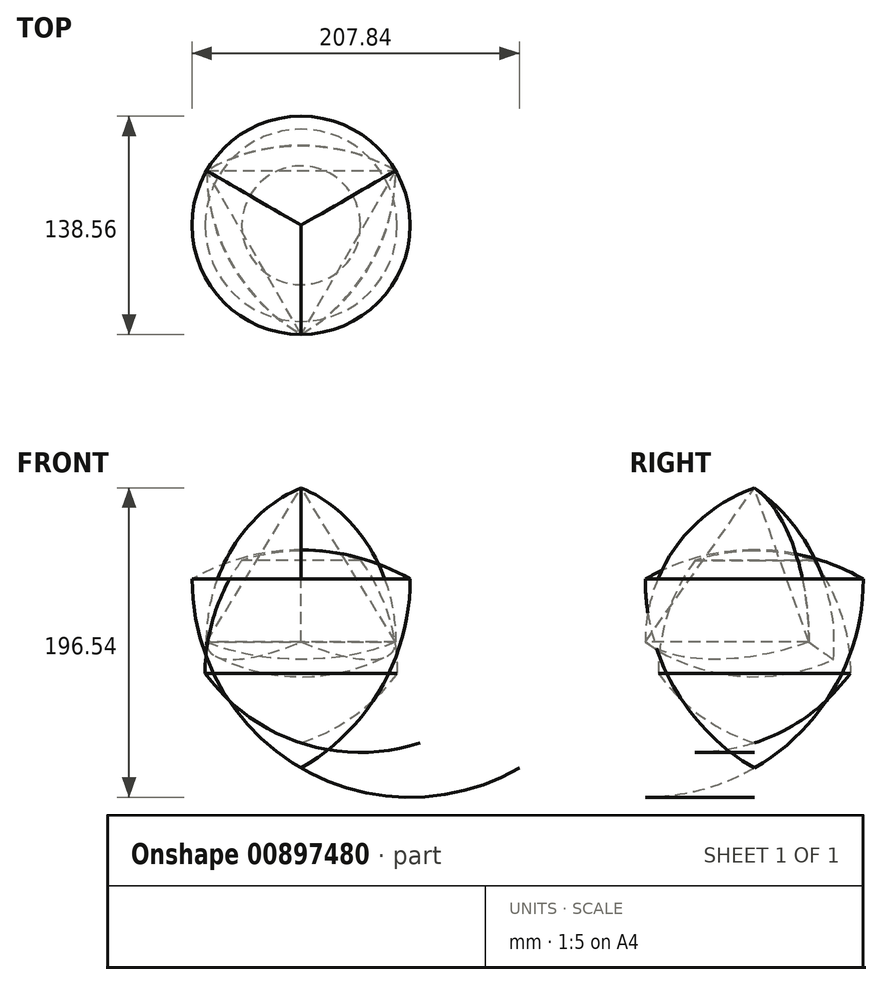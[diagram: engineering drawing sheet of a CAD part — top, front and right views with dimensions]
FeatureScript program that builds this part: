
annotation { "Feature Type Name" : "Feature", "Feature Type Description" : "" }
export const myFeature = defineFeature(function(context is Context, id is Id, definition is map)
    precondition{}
    {
        {
            var Q0;
            Q0=qCreatedBy(makeId("Front.planeOp"),FACE);
            var sketch = newSketch(context, id + "F0", { "sketchPlane" : qUnion([Q0])});
            skPoint(sketch, "E0.0.midPoint", {"position": v(0, 40) * mm});
            skArc(sketch, "E1", {"start": v(0, -80) * mm, "mid": v(50.72, -29.28) * mm, "end": v(69.28, 40) * mm});
            skArc(sketch, "E2", {"start": v(69.28, 40) * mm, "mid": v(0, 58.56) * mm, "end": v(-69.28, 40) * mm});
            skArc(sketch, "E3", {"start": v(-69.28, 40) * mm, "mid": v(-50.72, -29.28) * mm, "end": v(0, -80) * mm});
            skLineSegment(sketch, "E4", {"start": v(0, 58.56) * mm, "end": v(0, -80) * mm});
            skSolve(sketch);
        }
        {
            var Q0;
            Q0=qCreatedBy(makeId("Front.planeOp"),FACE);
            var sketch = newSketch(context, id + "F1", { "sketchPlane" : qUnion([Q0])});
            skLineSegment(sketch, "E5", {"start": v(0, 75.53) * mm, "end": v(0, -80.6) * mm, "construction": true});
            skSolve(sketch);
        }
        {
            var Q0;
            Q0=makeQuery(id+"F0.imprint","IMPRINT",FACE,{"disambiguationData":[TD([[makeQuery(id+"F0.imprint","IMPRINT",EDGE,{"derivedFrom":sQuery(id+"F0.wireOp",EDGE,"E1")}),1.0]])]});
            var Q1;
            Q1=sQuery(id+"F1.wireOp",EDGE,"E5");
            revolve(context, id + "F2", {"surfaceOperationType" : NewSurfaceOperationType.NEW, "entities" : qUnion([Q0]), "axis" : qUnion([Q1]), "revolveType" : RevolveType.FULL});
        }
        {
            var Q0;
            Q0=qCreatedBy(makeId("Front.planeOp"),FACE);
            var sketch = newSketch(context, id + "F3", { "sketchPlane" : qUnion([Q0])});
            skArc(sketch, "E6.cCircle", {"start": v(0, 51.88) * mm, "mid": v(-51.88, 0) * mm, "end": v(0, -51.88) * mm, "construction": true});
            skLineSegment(sketch, "E6.0", {"start": v(-37.7, 51.88) * mm, "end": v(0, 51.88) * mm});
            skLineSegment(sketch, "E6.3", {"start": v(0, -64.12) * mm, "end": v(-60.98, -19.81) * mm});
            skLineSegment(sketch, "E6.4", {"start": v(-60.98, -19.81) * mm, "end": v(-37.7, 51.88) * mm});
            skPoint(sketch, "E6.0.midPoint", {"position": v(0, 51.88) * mm});
            skArc(sketch, "E7", {"start": v(0, -64.12) * mm, "mid": v(34, -46.8) * mm, "end": v(60.98, -19.81) * mm});
            skArc(sketch, "E8.trimOffspring", {"start": v(60.98, -19.81) * mm, "mid": v(55.01, 17.88) * mm, "end": v(37.7, 51.88) * mm});
            skArc(sketch, "E9.trimOffspring", {"start": v(-60.98, -19.81) * mm, "mid": v(-34, -46.8) * mm, "end": v(0, -64.12) * mm});
            skArc(sketch, "E10.trimOffspring", {"start": v(-37.7, 51.88) * mm, "mid": v(-55.01, 17.88) * mm, "end": v(-60.98, -19.81) * mm});
            skArc(sketch, "E11.trimOffspring", {"start": v(37.7, 51.88) * mm, "mid": v(0, 57.85) * mm, "end": v(-37.7, 51.88) * mm});
            skLineSegment(sketch, "E12", {"start": v(0, -64.12) * mm, "end": v(0, 57.85) * mm});
            skSolve(sketch);
        }
        {
            var Q0;
            {var subQ5=sQuery(id+"F3.wireOp",EDGE,"E7");Q0=makeQuery(id+"F3.imprint","IMPRINT",FACE,{"disambiguationData":[TD([[makeQuery(id+"F3.imprint","IMPRINT",EDGE,{"derivedFrom":subQ5}),1.0]])]});}
            var Q1;
            Q1=sQuery(id+"F1.wireOp",EDGE,"E5");
            revolve(context, id + "F4", {"surfaceOperationType" : NewSurfaceOperationType.NEW, "entities" : qUnion([Q0]), "axis" : qUnion([Q1]), "revolveType" : RevolveType.FULL});
        }
        {
            var Q0;
            Q0=qCreatedBy(makeId("Top.planeOp"),FACE);
            var sketch = newSketch(context, id + "F5", { "sketchPlane" : qUnion([Q0])});
            skCircle(sketch, "E13.cCircle", {"center": v(0, 0) * mm, "radius": 34.64 * mm, "construction": true});
            skLineSegment(sketch, "E13.0", {"start": v(-60, 34.64) * mm, "end": v(60, 34.64) * mm});
            skLineSegment(sketch, "E13.1", {"start": v(60, 34.64) * mm, "end": v(0, -69.28) * mm});
            skLineSegment(sketch, "E13.2", {"start": v(0, -69.28) * mm, "end": v(-60, 34.64) * mm});
            skPoint(sketch, "E13.0.midPoint", {"position": v(0, 34.64) * mm});
            skSolve(sketch);
        }
        {
            var Q0;
            Q0=qCreatedBy(makeId("Right.planeOp"),FACE);
            var sketch = newSketch(context, id + "F6", { "sketchPlane" : qUnion([Q0])});
            skPoint(sketch, "E14", {"position": v(0, 97.98) * mm});
            skPoint(sketch, "E15.0", {"position": v(-69.28, 0) * mm});
            skSolve(sketch);
        }
        {
            var Q0;
            Q0=makeQuery(id+"F5.imprint","IMPRINT",FACE,{"disambiguationData":[TD([[makeQuery(id+"F5.imprint","IMPRINT",EDGE,{"derivedFrom":sQuery(id+"F5.wireOp",EDGE,"E13.0")}),-1.0]])]});
            var Q1;
            Q1=sQuery(id+"F6.wireOp",VERTEX,"E14");
            loft(context, id + "F7", {"sheetProfilesArray" : [{ "sheetProfileEntities" : qUnion([Q0]) }, { "sheetProfileEntities" : qUnion([Q1]) }]});
        }
        {
            var Q0;
            {var subQ0=sQuery(id+"F5.wireOp",EDGE,"E13.1");var subQ1=sQuery(id+"F5.wireOp",EDGE,"E13.2");var subQ2=sQuery(id+"F5.wireOp",EDGE,"E13.0");Q0=makeQuery(id+"F7.opLoft","SWEPT_FACE",FACE,{"disambiguationData":[OSD([subQ2,subQ0,subQ1]),TDD([makeQuery(id+"F5.imprint","INTERSECT",VERTEX,{"derivedFrom":[subQ2,subQ0]}),makeQuery(id+"F5.imprint","INTERSECT",VERTEX,{"derivedFrom":[subQ0,subQ1]}),makeQuery(id+"F5.imprint","IMPRINT",EDGE,{"derivedFrom":subQ0})])]});}
            var sketch = newSketch(context, id + "F8", { "sketchPlane" : qUnion([Q0])});
            skArc(sketch, "E16", {"start": v(56.74, -22.68) * mm, "mid": v(52.29, 39.28) * mm, "end": v(17.46, 90.71) * mm});
            skArc(sketch, "E17", {"start": v(17.46, 90.71) * mm, "mid": v(-33.97, 55.88) * mm, "end": v(-61.1, 0) * mm});
            skArc(sketch, "E18.trimOffspring", {"start": v(-61.1, 0) * mm, "mid": v(-5.22, -27.13) * mm, "end": v(56.74, -22.68) * mm});
            skSolve(sketch);
        }
        {
            var Q0;
            Q0=makeQuery(id+"F5.imprint","IMPRINT",FACE,{"disambiguationData":[TD([[makeQuery(id+"F5.imprint","IMPRINT",EDGE,{"derivedFrom":sQuery(id+"F5.wireOp",EDGE,"E13.0")}),-1.0]])]});
            var sketch = newSketch(context, id + "F9", { "sketchPlane" : qUnion([Q0])});
            skLineSegment(sketch, "E19.0.0", {"start": v(-60, 34.64) * mm, "end": v(0, -69.28) * mm});
            skLineSegment(sketch, "E19.0.1", {"start": v(0, -69.28) * mm, "end": v(60, 34.64) * mm});
            skLineSegment(sketch, "E19.0.2", {"start": v(60, 34.64) * mm, "end": v(-60, 34.64) * mm});
            skArc(sketch, "E20", {"start": v(0, -69.28) * mm, "mid": v(43.92, -25.36) * mm, "end": v(60, 34.64) * mm});
            skArc(sketch, "E21.trimOffspring", {"start": v(60, 34.64) * mm, "mid": v(0, 50.72) * mm, "end": v(-60, 34.64) * mm});
            skArc(sketch, "E22.trimOffspring", {"start": v(-60, 34.64) * mm, "mid": v(-43.92, -25.36) * mm, "end": v(0, -69.28) * mm});
            skSolve(sketch);
        }
        {
            var Q0;
            {var subQ0=sQuery(id+"F5.wireOp",EDGE,"E13.0");var subQ1=sQuery(id+"F5.wireOp",EDGE,"E13.1");var subQ2=sQuery(id+"F5.wireOp",EDGE,"E13.2");Q0=makeQuery(id+"F7.opLoft","SWEPT_FACE",FACE,{"disambiguationData":[OSD([subQ0,subQ1,subQ2]),TDD([makeQuery(id+"F5.imprint","INTERSECT",VERTEX,{"derivedFrom":[subQ0,subQ2]}),makeQuery(id+"F5.imprint","INTERSECT",VERTEX,{"derivedFrom":[subQ0,subQ1]}),makeQuery(id+"F5.imprint","IMPRINT",EDGE,{"derivedFrom":subQ0})])]});}
            var sketch = newSketch(context, id + "F10", { "sketchPlane" : qUnion([Q0])});
            skArc(sketch, "E23", {"start": v(0, 92.38) * mm, "mid": v(-43.92, 48.45) * mm, "end": v(-60, -11.55) * mm});
            skArc(sketch, "E24", {"start": v(-60, -11.55) * mm, "mid": v(0, -27.62) * mm, "end": v(60, -11.55) * mm});
            skArc(sketch, "E25.trimOffspring", {"start": v(60, -11.55) * mm, "mid": v(43.92, 48.45) * mm, "end": v(0, 92.38) * mm});
            skSolve(sketch);
        }
        {
            var Q0;
            Q0=makeQuery(id+"F10.imprint","IMPRINT",FACE,{"disambiguationData":[TD([[makeQuery(id+"F10.imprint","IMPRINT",EDGE,{"derivedFrom":sQuery(id+"F10.wireOp",EDGE,"E25.trimOffspring")}),1.0]])]});
            var Q1;
            Q1=sQuery(id+"F10.wireOp",EDGE,"E25.trimOffspring");
            var Q2;
            Q2=sQuery(id+"F8.wireOp",EDGE,"E17");
            var Q3;
            Q3=sQuery(id+"F9.wireOp",EDGE,"E22.trimOffspring");
            sweep(context, id + "F11", {"profiles" : qUnion([Q0]), "surfaceProfiles" : qUnion([Q1, Q2]), "path" : qUnion([Q3])});
        }
        {
            var Q0;
            {var subQ0=sQuery(id+"F5.wireOp",EDGE,"E13.1");var subQ1=sQuery(id+"F5.wireOp",EDGE,"E13.2");var subQ2=sQuery(id+"F5.wireOp",EDGE,"E13.0");Q0=makeQuery(id+"F7.opLoft","SWEPT_FACE",FACE,{"disambiguationData":[OSD([subQ2,subQ0,subQ1]),TDD([makeQuery(id+"F5.imprint","INTERSECT",VERTEX,{"derivedFrom":[subQ2,subQ0]}),makeQuery(id+"F5.imprint","INTERSECT",VERTEX,{"derivedFrom":[subQ0,subQ1]}),makeQuery(id+"F5.imprint","IMPRINT",EDGE,{"derivedFrom":subQ0})])]});}
            var sketch = newSketch(context, id + "F12", { "sketchPlane" : qUnion([Q0])});
            skCircle(sketch, "E26", {"center": v(-61.1, 0) * mm, "radius": 120 * mm});
            skLineSegment(sketch, "E27", {"start": v(-100.38, 113.39) * mm, "end": v(-21.82, -113.39) * mm});
            skSolve(sketch);
        }
        {
            var Q0;
            {var subQ0=sQuery(id+"F5.wireOp",EDGE,"E13.1");var subQ2=sQuery(id+"F5.wireOp",EDGE,"E13.0");var subQ3=sQuery(id+"F6.wireOp",VERTEX,"E14");Q0=makeQuery(id+"F12.imprint","IMPRINT",FACE,{"disambiguationData":[TD([[makeQuery(id+"F12.imprint","IMPRINT",EDGE,{"derivedFrom":makeQuery(id+"F7.opLoft","SWEPT_EDGE",EDGE,{"disambiguationData":[OSD([subQ2,subQ0,subQ3])]})}),1.0]])]});}
            var sketch = newSketch(context, id + "F13", { "sketchPlane" : qUnion([Q0])});
            skPoint(sketch, "E28.0", {"position": v(-61.1, 0) * mm});
            skLineSegment(sketch, "E29.0", {"start": v(56.74, -22.68) * mm, "end": v(17.46, 90.71) * mm});
            skLineSegment(sketch, "E30", {"start": v(-61.1, 0) * mm, "end": v(-74.02, 37.3) * mm});
            skSolve(sketch);
        }
        {
            var Q0;
            {var subQ0=sQuery(id+"F12.wireOp",EDGE,"E27");var subQ1=sQuery(id+"F12.wireOp",EDGE,"E26");var subQ2=makeQuery(id+"F12.imprint","INTERSECT",VERTEX,{"disambiguationData":[OD(0.0)],"derivedFrom":[subQ1,subQ0]});Q0=makeQuery(id+"F12.imprint","IMPRINT",FACE,{"disambiguationData":[TD([[makeQuery(id+"F12.imprint","IMPRINT",EDGE,{"disambiguationData":[TD([[subQ2,-1.0]])],"derivedFrom":subQ1}),1.0]])]});}
            var Q1;
            Q1=sQuery(id+"F13.wireOp",EDGE,"E30");
            revolve(context, id + "F14", {"surfaceOperationType" : NewSurfaceOperationType.NEW, "entities" : qUnion([Q0]), "axis" : qUnion([Q1]), "revolveType" : RevolveType.FULL});
        }
        {
            var Q0;
            {var subQ0=sQuery(id+"F5.wireOp",EDGE,"E13.0");var subQ1=sQuery(id+"F5.wireOp",EDGE,"E13.1");var subQ2=sQuery(id+"F5.wireOp",EDGE,"E13.2");Q0=makeQuery(id+"F7.opLoft","SWEPT_FACE",FACE,{"disambiguationData":[OSD([subQ0,subQ1,subQ2]),TDD([makeQuery(id+"F5.imprint","INTERSECT",VERTEX,{"derivedFrom":[subQ0,subQ2]}),makeQuery(id+"F5.imprint","INTERSECT",VERTEX,{"derivedFrom":[subQ0,subQ1]}),makeQuery(id+"F5.imprint","IMPRINT",EDGE,{"derivedFrom":subQ0})])]});}
            var sketch = newSketch(context, id + "F15", { "sketchPlane" : qUnion([Q0])});
            skCircle(sketch, "E31", {"center": v(-60, -11.55) * mm, "radius": 120 * mm});
            skLineSegment(sketch, "E32", {"start": v(0, 92.38) * mm, "end": v(-120, -115.47) * mm});
            skSolve(sketch);
        }
        {
            var Q0;
            {var subQ0=sQuery(id+"F15.wireOp",EDGE,"E32");var subQ1=sQuery(id+"F15.wireOp",EDGE,"E31");var subQ5=makeQuery(id+"F15.imprint","INTERSECT",VERTEX,{"derivedFrom":[subQ1,subQ0]});Q0=makeQuery(id+"F15.imprint","IMPRINT",FACE,{"disambiguationData":[TD([[makeQuery(id+"F15.imprint","IMPRINT",EDGE,{"disambiguationData":[TD([[subQ5,1.0]])],"derivedFrom":subQ1}),1.0]])]});}
            var Q1;
            Q1=sQuery(id+"F15.wireOp",EDGE,"E32");
            revolve(context, id + "F16", {"surfaceOperationType" : NewSurfaceOperationType.NEW, "entities" : qUnion([Q0]), "axis" : qUnion([Q1]), "revolveType" : RevolveType.FULL});
        }
        {
            var Q0;
            {var subQ0=sQuery(id+"F5.wireOp",EDGE,"E13.2");var subQ1=sQuery(id+"F5.wireOp",EDGE,"E13.1");var subQ2=sQuery(id+"F5.wireOp",EDGE,"E13.0");Q0=makeQuery(id+"F7.opLoft","SWEPT_FACE",FACE,{"disambiguationData":[OSD([subQ2,subQ1,subQ0]),TDD([makeQuery(id+"F5.imprint","INTERSECT",VERTEX,{"derivedFrom":[subQ2,subQ0]}),makeQuery(id+"F5.imprint","INTERSECT",VERTEX,{"derivedFrom":[subQ1,subQ0]}),makeQuery(id+"F5.imprint","IMPRINT",EDGE,{"derivedFrom":subQ0})])]});}
            var sketch = newSketch(context, id + "F17", { "sketchPlane" : qUnion([Q0])});
            skCircle(sketch, "E33", {"center": v(-56.74, -22.68) * mm, "radius": 120 * mm});
            skLineSegment(sketch, "E34", {"start": v(-17.46, 90.71) * mm, "end": v(-96.02, -136.07) * mm});
            skSolve(sketch);
        }
        {
            var Q0;
            {var subQ0=sQuery(id+"F17.wireOp",EDGE,"E34");var subQ1=sQuery(id+"F17.wireOp",EDGE,"E33");var subQ5=makeQuery(id+"F17.imprint","INTERSECT",VERTEX,{"derivedFrom":[subQ1,subQ0]});Q0=makeQuery(id+"F17.imprint","IMPRINT",FACE,{"disambiguationData":[TD([[makeQuery(id+"F17.imprint","IMPRINT",EDGE,{"disambiguationData":[TD([[subQ5,1.0]])],"derivedFrom":subQ1}),1.0]])]});}
            var Q1;
            Q1=sQuery(id+"F17.wireOp",EDGE,"E34");
            revolve(context, id + "F18", {"surfaceOperationType" : NewSurfaceOperationType.NEW, "entities" : qUnion([Q0]), "axis" : qUnion([Q1]), "revolveType" : RevolveType.FULL});
        }
        {
            var Q0;
            {var subQ0=sQuery(id+"F5.wireOp",EDGE,"E13.2");var subQ1=sQuery(id+"F5.wireOp",EDGE,"E13.1");var subQ2=sQuery(id+"F5.wireOp",EDGE,"E13.0");Q0=makeQuery(id+"F7.opLoft","SWEPT_FACE",FACE,{"disambiguationData":[OSD([subQ2,subQ1,subQ0]),TDD([makeQuery(id+"F5.imprint","INTERSECT",VERTEX,{"derivedFrom":[subQ2,subQ0]}),makeQuery(id+"F5.imprint","INTERSECT",VERTEX,{"derivedFrom":[subQ1,subQ0]}),makeQuery(id+"F5.imprint","IMPRINT",EDGE,{"derivedFrom":subQ0})])]});}
            var sketch = newSketch(context, id + "F19", { "sketchPlane" : qUnion([Q0])});
            skCircle(sketch, "E35", {"center": v(-17.46, 90.71) * mm, "radius": 120 * mm});
            skLineSegment(sketch, "E36", {"start": v(-56.74, -22.68) * mm, "end": v(21.82, 204.1) * mm});
            skSolve(sketch);
        }
        {
            var Q0;
            {var subQ0=sQuery(id+"F19.wireOp",EDGE,"E36");var subQ1=sQuery(id+"F19.wireOp",EDGE,"E35");var subQ6=makeQuery(id+"F19.imprint","INTERSECT",VERTEX,{"derivedFrom":[subQ1,subQ0]});Q0=makeQuery(id+"F19.imprint","IMPRINT",FACE,{"disambiguationData":[TD([[makeQuery(id+"F19.imprint","IMPRINT",EDGE,{"disambiguationData":[TD([[subQ6,1.0]])],"derivedFrom":subQ0}),1.0]])]});}
            var Q1;
            Q1=sQuery(id+"F19.wireOp",EDGE,"E36");
            revolve(context, id + "F20", {"surfaceOperationType" : NewSurfaceOperationType.NEW, "entities" : qUnion([Q0]), "axis" : qUnion([Q1]), "revolveType" : RevolveType.FULL});
        }
        {
            var Q0;
            Q0=makeQuery(id+"F14.opRevolve","SWEPT_BODY",BODY,{"disambiguationData":[OSD([sQuery(id+"F12.wireOp",EDGE,"E26"),sQuery(id+"F12.wireOp",EDGE,"E27")])]});
            var Q1;
            Q1=makeQuery(id+"F16.opRevolve","SWEPT_BODY",BODY,{"disambiguationData":[OSD([sQuery(id+"F15.wireOp",EDGE,"E31"),sQuery(id+"F15.wireOp",EDGE,"E32")])]});
            var Q2;
            Q2=makeQuery(id+"F18.opRevolve","SWEPT_BODY",BODY,{"disambiguationData":[OSD([sQuery(id+"F17.wireOp",EDGE,"E33"),sQuery(id+"F17.wireOp",EDGE,"E34")])]});
            var Q3;
            Q3=makeQuery(id+"F20.opRevolve","SWEPT_BODY",BODY,{"disambiguationData":[OSD([sQuery(id+"F19.wireOp",EDGE,"E35"),sQuery(id+"F19.wireOp",EDGE,"E36")])]});
            booleanBodies(context, id + "F21", {"operationType" : BooleanOperationType.INTERSECTION, "tools" : qUnion([Q0, Q1, Q2, Q3])});
        }
        {
            var Q0;
            Q0=makeQuery(id+"F11.opSweep","SWEPT_BODY",BODY,{"disambiguationData":[OSD([sQuery(id+"F5.wireOp",EDGE,"E13.0"),sQuery(id+"F5.wireOp",EDGE,"E13.2"),sQuery(id+"F6.wireOp",VERTEX,"E14"),sQuery(id+"F9.wireOp",EDGE,"E22.trimOffspring"),sQuery(id+"F10.wireOp",EDGE,"E25.trimOffspring")])]});
            deleteBodies(context, id + "F22", {"entities" : qUnion([Q0])});
        }
    });
